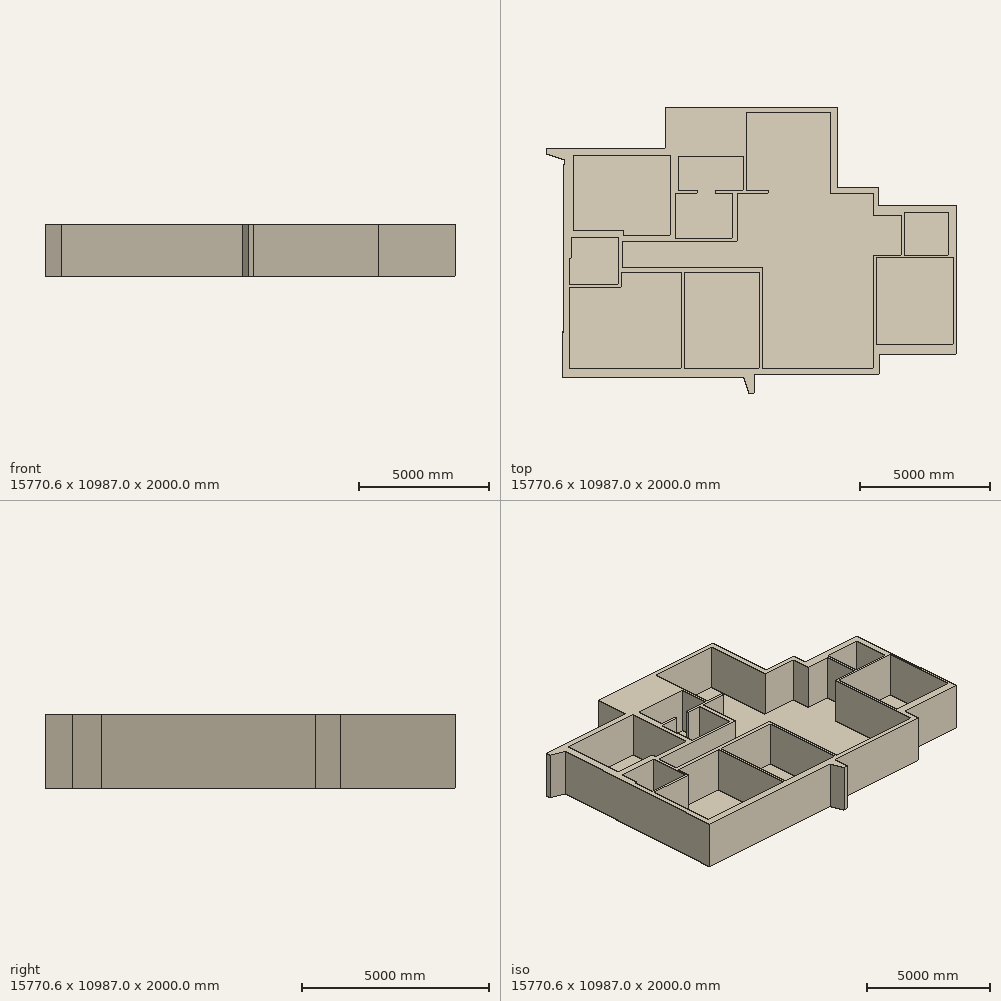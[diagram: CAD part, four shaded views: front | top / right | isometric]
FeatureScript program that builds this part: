
annotation { "Feature Type Name" : "Feature", "Feature Type Description" : "" }
export const myFeature = defineFeature(function(context is Context, id is Id, definition is map)
    precondition{}
    {
        {
            var Q0;
            Q0=qCreatedBy(makeId("Top.planeOp"),FACE);
            var sketch = newSketch(context, id + "F0", { "sketchPlane" : qUnion([Q0])});
            skLineSegment(sketch, "E0", {"start": v(-7881.53, 4879.5) * mm, "end": v(-3292.98, 4879.5) * mm});
            skLineSegment(sketch, "E1", {"start": v(-3292.98, 4879.5) * mm, "end": v(-3292.98, 6455) * mm});
            skLineSegment(sketch, "E2", {"start": v(-3292.98, 6455) * mm, "end": v(3301.65, 6455) * mm});
            skLineSegment(sketch, "E3", {"start": v(-7881.53, 4879.5) * mm, "end": v(-7881.53, 4675.85) * mm});
            skLineSegment(sketch, "E4", {"start": v(-7881.53, 4675.85) * mm, "end": v(-7206.92, 4455.3) * mm});
            skLineSegment(sketch, "E5", {"start": v(-7206.92, 4455.3) * mm, "end": v(-7257.02, -3915) * mm});
            skLineSegment(sketch, "E6", {"start": v(-7257.02, -3915) * mm, "end": v(-295.07, -3915) * mm});
            skLineSegment(sketch, "E7", {"start": v(-295.07, -3915) * mm, "end": v(-89.05, -4531.98) * mm});
            skLineSegment(sketch, "E8", {"start": v(-89.05, -4531.98) * mm, "end": v(107.43, -4531.98) * mm});
            skLineSegment(sketch, "E9", {"start": v(107.43, -3804.12) * mm, "end": v(107.43, -4531.98) * mm});
            skLineSegment(sketch, "E10", {"start": v(107.43, -3804.12) * mm, "end": v(4915.44, -3804.12) * mm});
            skLineSegment(sketch, "E11", {"start": v(4915.44, -3804.12) * mm, "end": v(4915.44, -3030.1) * mm});
            skLineSegment(sketch, "E12", {"start": v(4915.44, -3030.1) * mm, "end": v(7889.08, -3030.1) * mm});
            skLineSegment(sketch, "E13", {"start": v(7889.08, -3030.1) * mm, "end": v(7872.6, 2703.32) * mm});
            skLineSegment(sketch, "E14", {"start": v(7872.6, 2703.32) * mm, "end": v(4897.84, 2703.32) * mm});
            skLineSegment(sketch, "E15", {"start": v(4897.84, 2703.32) * mm, "end": v(4897.84, 3374.24) * mm});
            skLineSegment(sketch, "E16", {"start": v(4897.84, 3374.24) * mm, "end": v(3311, 3369.68) * mm});
            skLineSegment(sketch, "E17", {"start": v(3311, 3369.68) * mm, "end": v(3301.65, 6455) * mm});
            skSolve(sketch);
        }
        {
            var Q0;
            Q0=makeQuery(id+"F0.imprint","IMPRINT",FACE,{"disambiguationData":[TD([[makeQuery(id+"F0.imprint","IMPRINT",EDGE,{"derivedFrom":sQuery(id+"F0.wireOp",EDGE,"E0")}),-1.0]])]});
            extrude(context, id + "F1", {"entities" : qUnion([Q0]), "depth" : 2000 * mm, "offsetDistance" : 25 * mm});
        }
        {
            var Q0;
            Q0=makeQuery(id+"F1.opExtrude","CAP_FACE",FACE,{"disambiguationData":[OSD([sQuery(id+"F0.wireOp",EDGE,"E0"),sQuery(id+"F0.wireOp",EDGE,"E1"),sQuery(id+"F0.wireOp",EDGE,"E2"),sQuery(id+"F0.wireOp",EDGE,"E3"),sQuery(id+"F0.wireOp",EDGE,"E4"),sQuery(id+"F0.wireOp",EDGE,"E5"),sQuery(id+"F0.wireOp",EDGE,"E6"),sQuery(id+"F0.wireOp",EDGE,"E7"),sQuery(id+"F0.wireOp",EDGE,"E8"),sQuery(id+"F0.wireOp",EDGE,"E9"),sQuery(id+"F0.wireOp",EDGE,"E10"),sQuery(id+"F0.wireOp",EDGE,"E11"),sQuery(id+"F0.wireOp",EDGE,"E12"),sQuery(id+"F0.wireOp",EDGE,"E13"),sQuery(id+"F0.wireOp",EDGE,"E14"),sQuery(id+"F0.wireOp",EDGE,"E15"),sQuery(id+"F0.wireOp",EDGE,"E16"),sQuery(id+"F0.wireOp",EDGE,"E17")])],"isStart":false});
            var sketch = newSketch(context, id + "F2", { "sketchPlane" : qUnion([Q0])});
            skLineSegment(sketch, "E18", {"start": v(-6850.23, 4621.53) * mm, "end": v(-3130.82, 4621.53) * mm});
            skLineSegment(sketch, "E19", {"start": v(-3130.82, 4621.53) * mm, "end": v(-3130.82, 1536.36) * mm});
            skLineSegment(sketch, "E20", {"start": v(-3130.82, 1536.36) * mm, "end": v(-4909.3, 1536.36) * mm});
            skLineSegment(sketch, "E21", {"start": v(-4909.3, 1536.36) * mm, "end": v(-4909.3, 1749.27) * mm});
            skLineSegment(sketch, "E22", {"start": v(-4909.3, 1749.27) * mm, "end": v(-6850.61, 1749.27) * mm});
            skLineSegment(sketch, "E23", {"start": v(-6850.61, 1749.27) * mm, "end": v(-6850.23, 4621.53) * mm});
            skLineSegment(sketch, "E24", {"start": v(-6904.44, 1465.48) * mm, "end": v(-5108.4, 1465.48) * mm});
            skLineSegment(sketch, "E25", {"start": v(-5108.4, 1465.48) * mm, "end": v(-5108.4, -361.29) * mm});
            skLineSegment(sketch, "E26", {"start": v(-5108.4, -361.29) * mm, "end": v(-6996.63, -361.29) * mm});
            skLineSegment(sketch, "E27", {"start": v(-6996.63, -361.29) * mm, "end": v(-6996.63, 663.07) * mm});
            skLineSegment(sketch, "E28", {"start": v(-6996.63, 663.07) * mm, "end": v(-6904.44, 663.07) * mm});
            skLineSegment(sketch, "E29", {"start": v(-6904.44, 663.07) * mm, "end": v(-6904.44, 1465.48) * mm});
            skLineSegment(sketch, "E30", {"start": v(-6989.62, -463.98) * mm, "end": v(-6989.62, -3587.92) * mm});
            skLineSegment(sketch, "E31", {"start": v(-6989.62, -3587.92) * mm, "end": v(-2671.23, -3587.92) * mm});
            skLineSegment(sketch, "E32", {"start": v(-2671.23, -3587.92) * mm, "end": v(-2671.23, 133.24) * mm});
            skLineSegment(sketch, "E33", {"start": v(-2671.23, 133.24) * mm, "end": v(-5002.7, 133.24) * mm});
            skLineSegment(sketch, "E34", {"start": v(-5002.7, 133.24) * mm, "end": v(-5002.7, -469.72) * mm});
            skLineSegment(sketch, "E35", {"start": v(-5002.7, -469.72) * mm, "end": v(-6989.62, -463.98) * mm});
            skLineSegment(sketch, "E36", {"start": v(307.5, -3587.92) * mm, "end": v(-2570.52, -3587.92) * mm});
            skLineSegment(sketch, "E37", {"start": v(-2570.52, -3587.92) * mm, "end": v(-2570.52, 133.82) * mm});
            skLineSegment(sketch, "E38", {"start": v(-2570.52, 133.82) * mm, "end": v(308.3, 133.82) * mm});
            skLineSegment(sketch, "E39", {"start": v(308.3, 133.82) * mm, "end": v(307.5, -3587.92) * mm});
            skLineSegment(sketch, "E40", {"start": v(4698.2, -3587.92) * mm, "end": v(425.76, -3587.92) * mm});
            skLineSegment(sketch, "E41", {"start": v(425.76, -3587.92) * mm, "end": v(425.76, 297.86) * mm});
            skLineSegment(sketch, "E42", {"start": v(425.76, 297.86) * mm, "end": v(-4957.83, 297.86) * mm});
            skLineSegment(sketch, "E43", {"start": v(-4957.83, 297.86) * mm, "end": v(-4957.83, 1322.83) * mm});
            skLineSegment(sketch, "E44", {"start": v(-4957.83, 1322.83) * mm, "end": v(-528.64, 1322.83) * mm});
            skLineSegment(sketch, "E45", {"start": v(-528.64, 1322.83) * mm, "end": v(-528.23, 3169.38) * mm});
            skLineSegment(sketch, "E46", {"start": v(-528.23, 3169.38) * mm, "end": v(639.95, 3169.38) * mm});
            skLineSegment(sketch, "E47", {"start": v(639.95, 3169.38) * mm, "end": v(639.95, 3283.13) * mm});
            skLineSegment(sketch, "E48", {"start": v(639.95, 3283.13) * mm, "end": v(-181, 3283.13) * mm});
            skLineSegment(sketch, "E49", {"start": v(-181, 3283.13) * mm, "end": v(-180.36, 6255.9) * mm});
            skLineSegment(sketch, "E50", {"start": v(-180.36, 6255.9) * mm, "end": v(3043.27, 6255.9) * mm});
            skLineSegment(sketch, "E51", {"start": v(3043.27, 6255.9) * mm, "end": v(3043.27, 3167.16) * mm});
            skLineSegment(sketch, "E52", {"start": v(3043.27, 3167.16) * mm, "end": v(4677.54, 3167.16) * mm});
            skLineSegment(sketch, "E53", {"start": v(4677.54, 3167.16) * mm, "end": v(4677.54, 2303.06) * mm});
            skLineSegment(sketch, "E54", {"start": v(4677.54, 2303.06) * mm, "end": v(5782.95, 2303.06) * mm});
            skLineSegment(sketch, "E55", {"start": v(5782.95, 2303.06) * mm, "end": v(5782.95, 771.24) * mm});
            skLineSegment(sketch, "E56", {"start": v(5782.95, 771.24) * mm, "end": v(4677.54, 771.24) * mm});
            skLineSegment(sketch, "E57", {"start": v(4677.54, 771.24) * mm, "end": v(4698.2, -3587.92) * mm});
            skLineSegment(sketch, "E58", {"start": v(4806.88, 676.07) * mm, "end": v(7775.28, 676.07) * mm});
            skLineSegment(sketch, "E59", {"start": v(7775.28, 676.07) * mm, "end": v(7775.28, -2664.14) * mm});
            skLineSegment(sketch, "E60", {"start": v(7775.28, -2664.14) * mm, "end": v(4800.88, -2664.14) * mm});
            skLineSegment(sketch, "E61", {"start": v(4800.88, -2664.14) * mm, "end": v(4806.88, 676.07) * mm});
            skLineSegment(sketch, "E62", {"start": v(5895.87, 2413.84) * mm, "end": v(7582.44, 2413.84) * mm});
            skLineSegment(sketch, "E63", {"start": v(7582.44, 2413.84) * mm, "end": v(7582.44, 771.24) * mm});
            skLineSegment(sketch, "E64", {"start": v(7582.44, 771.24) * mm, "end": v(5892.3, 771.24) * mm});
            skLineSegment(sketch, "E65", {"start": v(5892.3, 771.24) * mm, "end": v(5895.87, 2413.84) * mm});
            skLineSegment(sketch, "E66", {"start": v(-2910.83, 1427.8) * mm, "end": v(-737.83, 1427.8) * mm});
            skLineSegment(sketch, "E67", {"start": v(-737.83, 1427.8) * mm, "end": v(-737.83, 3169.38) * mm});
            skLineSegment(sketch, "E68", {"start": v(-737.83, 3169.38) * mm, "end": v(-1399.4, 3169.38) * mm});
            skLineSegment(sketch, "E69", {"start": v(-1399.4, 3169.38) * mm, "end": v(-1399.4, 3283.13) * mm});
            skLineSegment(sketch, "E70", {"start": v(-1399.4, 3283.13) * mm, "end": v(-295.07, 3283.13) * mm});
            skLineSegment(sketch, "E71", {"start": v(-295.07, 3283.13) * mm, "end": v(-295.07, 4593.69) * mm});
            skLineSegment(sketch, "E72", {"start": v(-295.07, 4593.69) * mm, "end": v(-2812.78, 4593.69) * mm});
            skLineSegment(sketch, "E73", {"start": v(-2812.78, 4593.69) * mm, "end": v(-2812.78, 3283.13) * mm});
            skLineSegment(sketch, "E74", {"start": v(-2812.78, 3283.13) * mm, "end": v(-2076.15, 3283.13) * mm});
            skLineSegment(sketch, "E75", {"start": v(-2076.15, 3283.13) * mm, "end": v(-2076.15, 3167.16) * mm});
            skLineSegment(sketch, "E76", {"start": v(-2076.15, 3167.16) * mm, "end": v(-2923.76, 3169.38) * mm});
            skLineSegment(sketch, "E77", {"start": v(-2923.76, 3169.38) * mm, "end": v(-2910.83, 1427.8) * mm});
            skSolve(sketch);
        }
        {
            var Q0;
            Q0=makeQuery(id+"F2.imprint","IMPRINT",FACE,{"disambiguationData":[TD([[makeQuery(id+"F2.imprint","IMPRINT",EDGE,{"derivedFrom":sQuery(id+"F2.wireOp",EDGE,"E18")}),-1.0]])]});
            var Q1;
            Q1=makeQuery(id+"F2.imprint","IMPRINT",FACE,{"disambiguationData":[TD([[makeQuery(id+"F2.imprint","IMPRINT",EDGE,{"derivedFrom":sQuery(id+"F2.wireOp",EDGE,"E24")}),-1.0]])]});
            var Q2;
            Q2=makeQuery(id+"F2.imprint","IMPRINT",FACE,{"disambiguationData":[TD([[makeQuery(id+"F2.imprint","IMPRINT",EDGE,{"derivedFrom":sQuery(id+"F2.wireOp",EDGE,"E40")}),-1.0]])]});
            var Q3;
            Q3=makeQuery(id+"F2.imprint","IMPRINT",FACE,{"disambiguationData":[TD([[makeQuery(id+"F2.imprint","IMPRINT",EDGE,{"derivedFrom":sQuery(id+"F2.wireOp",EDGE,"E58")}),-1.0]])]});
            var Q4;
            Q4=makeQuery(id+"F2.imprint","IMPRINT",FACE,{"disambiguationData":[TD([[makeQuery(id+"F2.imprint","IMPRINT",EDGE,{"derivedFrom":sQuery(id+"F2.wireOp",EDGE,"E62")}),-1.0]])]});
            var Q5;
            Q5=makeQuery(id+"F2.imprint","IMPRINT",FACE,{"disambiguationData":[TD([[makeQuery(id+"F2.imprint","IMPRINT",EDGE,{"derivedFrom":sQuery(id+"F2.wireOp",EDGE,"E66")}),1.0]])]});
            var Q6;
            Q6=makeQuery(id+"F2.imprint","IMPRINT",FACE,{"disambiguationData":[TD([[makeQuery(id+"F2.imprint","IMPRINT",EDGE,{"derivedFrom":sQuery(id+"F2.wireOp",EDGE,"E30")}),1.0]])]});
            var Q7;
            Q7=makeQuery(id+"F2.imprint","IMPRINT",FACE,{"disambiguationData":[TD([[makeQuery(id+"F2.imprint","IMPRINT",EDGE,{"derivedFrom":sQuery(id+"F2.wireOp",EDGE,"E36")}),-1.0]])]});
            extrude(context, id + "F3", {"entities" : qUnion([Q0, Q1, Q2, Q3, Q4, Q5, Q6, Q7]), "operationType" : NewBodyOperationType.REMOVE, "oppositeDirection" : true, "depth" : 1900 * mm, "offsetDistance" : 25 * mm});
        }
    });
